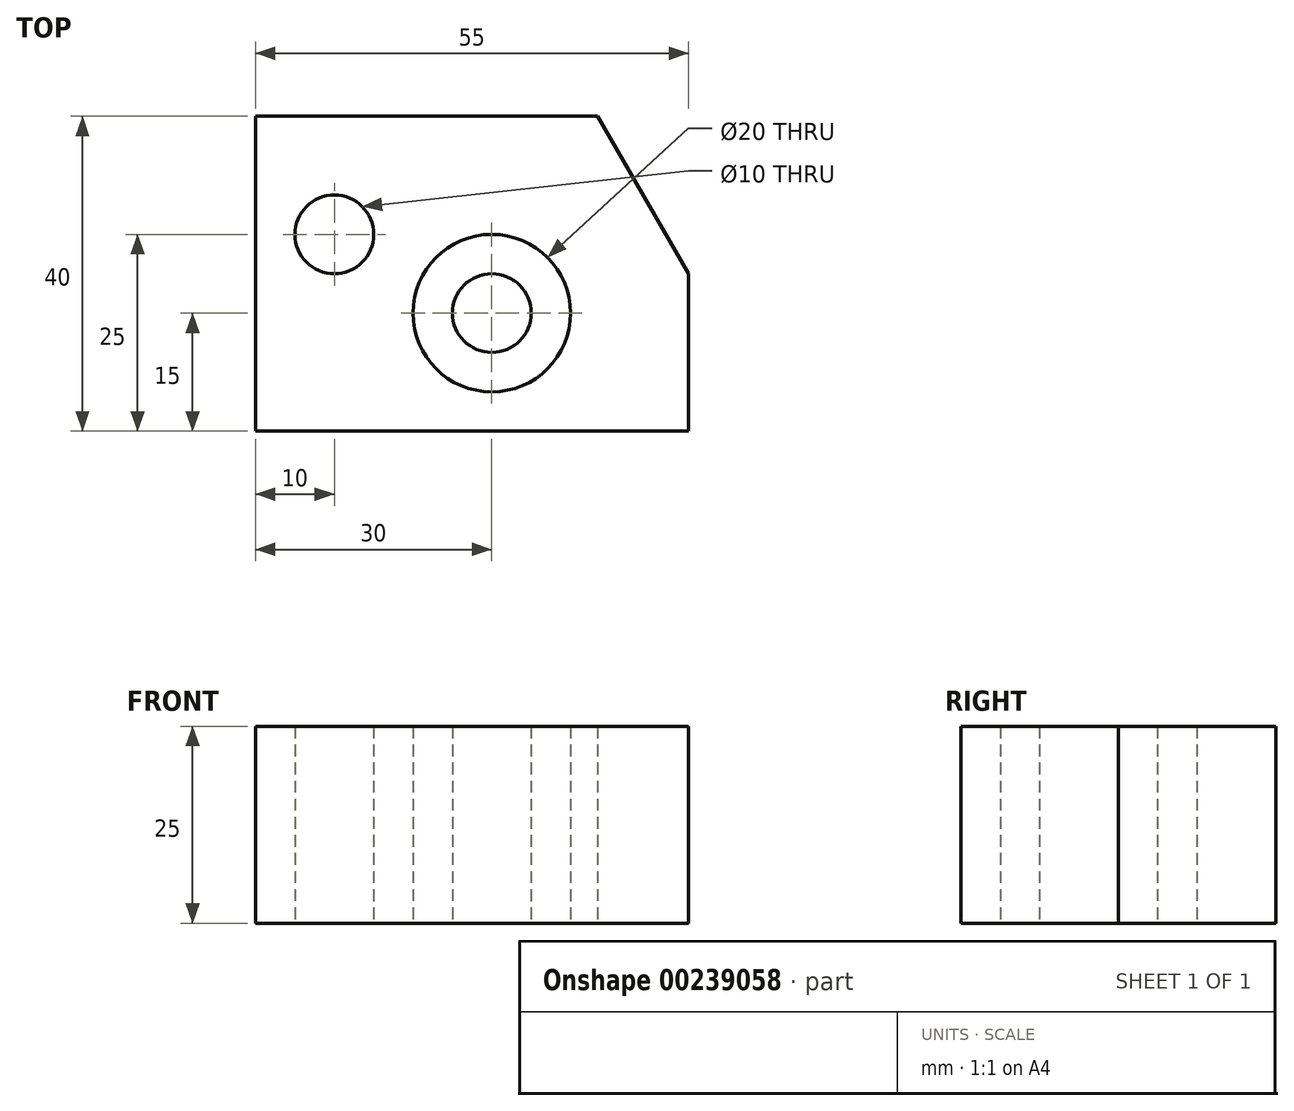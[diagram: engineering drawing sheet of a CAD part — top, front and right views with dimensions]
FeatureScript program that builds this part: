
annotation { "Feature Type Name" : "Feature", "Feature Type Description" : "" }
export const myFeature = defineFeature(function(context is Context, id is Id, definition is map)
    precondition{}
    {
        {
            var Q0;
            Q0=qCreatedBy(makeId("Top.planeOp"),FACE);
            var sketch = newSketch(context, id + "F0", { "sketchPlane" : qUnion([Q0])});
            skCircle(sketch, "E0", {"center": v(0, 0) * mm, "radius": 5 * mm});
            skCircle(sketch, "E1", {"center": v(0, 0) * mm, "radius": 10 * mm});
            skLineSegment(sketch, "E2", {"start": v(0, 0) * mm, "end": v(40.17, 0) * mm, "construction": true});
            skLineSegment(sketch, "E3", {"start": v(25, -15) * mm, "end": v(-30, -15) * mm});
            skLineSegment(sketch, "E4", {"start": v(0, 0) * mm, "end": v(0, -15) * mm, "construction": true});
            skLineSegment(sketch, "E5", {"start": v(25, -15) * mm, "end": v(25, 5) * mm});
            skLineSegment(sketch, "E6", {"start": v(25, 5) * mm, "end": v(25, 25) * mm, "construction": true});
            skLineSegment(sketch, "E7", {"start": v(-30, -15) * mm, "end": v(-30, 25) * mm});
            skLineSegment(sketch, "E8", {"start": v(-30, 25) * mm, "end": v(25, 25) * mm});
            skLineSegment(sketch, "E9", {"start": v(25, 5) * mm, "end": v(13.45, 25) * mm});
            skLineSegment(sketch, "E10", {"start": v(-30, -15) * mm, "end": v(-30, 10) * mm});
            skLineSegment(sketch, "E11", {"start": v(-30, 25) * mm, "end": v(-20, 25) * mm});
            skLineSegment(sketch, "E12", {"start": v(-30, 10) * mm, "end": v(-20, 10) * mm, "construction": true});
            skLineSegment(sketch, "E13", {"start": v(-20, 10) * mm, "end": v(-20, 25) * mm, "construction": true});
            skCircle(sketch, "E14", {"center": v(-20, 10) * mm, "radius": 5 * mm});
            skSolve(sketch);
        }
        {
            var Q0;
            Q0=makeQuery(id+"F0.imprint","IMPRINT",FACE,{"disambiguationData":[TD([[makeQuery(id+"F0.imprint","IMPRINT",EDGE,{"derivedFrom":sQuery(id+"F0.wireOp",EDGE,"E0")}),1.0]])]});
            var Q1;
            Q1=makeQuery(id+"F0.imprint","IMPRINT",FACE,{"disambiguationData":[TD([[makeQuery(id+"F0.imprint","IMPRINT",EDGE,{"derivedFrom":sQuery(id+"F0.wireOp",EDGE,"E1")}),-1.0]])]});
            extrude(context, id + "F1", {"entities" : qUnion([Q0, Q1]), "depth" : 25 * mm});
        }
    });
